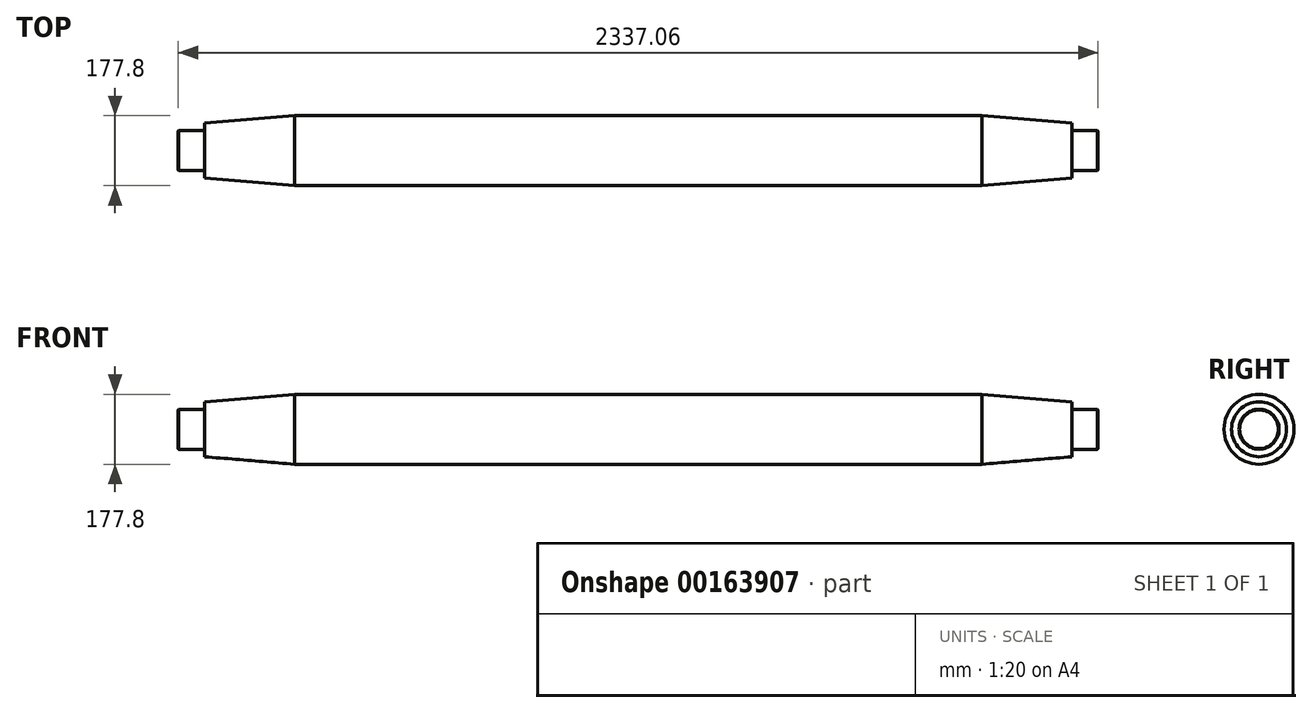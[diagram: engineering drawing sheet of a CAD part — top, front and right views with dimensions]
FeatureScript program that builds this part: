
annotation { "Feature Type Name" : "Feature", "Feature Type Description" : "" }
export const myFeature = defineFeature(function(context is Context, id is Id, definition is map)
    precondition{}
    {
        {
            var Q0;
            Q0=qCreatedBy(makeId("Right.planeOp"),FACE);
            var sketch = newSketch(context, id + "F0", { "sketchPlane" : qUnion([Q0])});
            skCircle(sketch, "E0", {"center": v(0, 0) * mm, "radius": 88.9 * mm});
            skSolve(sketch);
        }
        {
            var Q0;
            Q0 = qSketchRegion(id + "F0", true);
            extrude(context, id + "F1", {"entities" : qUnion([Q0]), "endBound" : BoundingType.SYMMETRIC, "depth" : 1746.25 * mm});
        }
        {
            var Q0;
            Q0=makeQuery(id+"F1.opExtrude","CAP_FACE",FACE,{"disambiguationData":[OSD([sQuery(id+"F0.wireOp",EDGE,"E0")])],"isStart":false});
            cPlane(context, id + "F2", {"entities" : qUnion([Q0]), "cplaneType" : CPlaneType.OFFSET, "offset" : 228.6 * mm, "width" : 152.4 * mm, "height" : 152.4 * mm});
        }
        {
            var Q0;
            Q0=qCreatedBy(id+"F2.planeOp",FACE);
            var sketch = newSketch(context, id + "F3", { "sketchPlane" : qUnion([Q0])});
            skCircle(sketch, "E1", {"center": v(0, 0) * mm, "radius": 69.85 * mm});
            skSolve(sketch);
        }
        {
            var Q1;
            Q1=makeQuery(id+"F1.opExtrude","CAP_FACE",FACE,{"disambiguationData":[OSD([sQuery(id+"F0.wireOp",EDGE,"E0")])],"isStart":false});
            var Q2;
            Q2=makeQuery(id+"F3.imprint","IMPRINT",FACE,{"disambiguationData":[TD([[makeQuery(id+"F3.imprint","IMPRINT",EDGE,{"derivedFrom":sQuery(id+"F3.wireOp",EDGE,"E1")}),1.0]])]});
            loft(context, id + "F4", {"sheetProfilesArray" : [{ "sheetProfileEntities" : qUnion([Q1]) }, { "sheetProfileEntities" : qUnion([Q2]) }]});
        }
        {
            var Q0;
            Q0=makeQuery(id+"F4.opLoft","CAP_FACE",FACE,{"disambiguationData":[OSD([makeQuery(id+"F3.imprint","IMPRINT",FACE,{"disambiguationData":[TD([[makeQuery(id+"F3.imprint","IMPRINT",EDGE,{"derivedFrom":sQuery(id+"F3.wireOp",EDGE,"E1")}),1.0]])]})])],"isStart":true});
            var sketch = newSketch(context, id + "F5", { "sketchPlane" : qUnion([Q0])});
            skCircle(sketch, "E2", {"center": v(0, 0) * mm, "radius": 50.8 * mm});
            skSolve(sketch);
        }
        {
            var Q0;
            Q0=makeQuery(id+"F5.imprint","IMPRINT",FACE,{"disambiguationData":[TD([[makeQuery(id+"F5.imprint","IMPRINT",EDGE,{"derivedFrom":sQuery(id+"F5.wireOp",EDGE,"E2")}),1.0]])]});
            extrude(context, id + "F6", {"entities" : qUnion([Q0]), "operationType" : NewBodyOperationType.ADD, "depth" : 66.8 * mm});
        }
        {
            var Q0;
            Q0=makeQuery(id+"F6.opExtrude","CAP_FACE",FACE,{"disambiguationData":[OSD([sQuery(id+"F5.wireOp",EDGE,"E2")])],"isStart":false});
            chamfer(context, id + "F7", {"entities" : qUnion([Q0]), "width" : 1.52 * mm, "tangentPropagation" : true});
        }
        {
            var Q0;
            Q0=makeQuery(id+"F4.opLoft","SWEPT_BODY",BODY,{"disambiguationData":[OSD([sQuery(id+"F0.wireOp",EDGE,"E0"),makeQuery(id+"F3.imprint","IMPRINT",FACE,{"disambiguationData":[TD([[makeQuery(id+"F3.imprint","IMPRINT",EDGE,{"derivedFrom":sQuery(id+"F3.wireOp",EDGE,"E1")}),1.0]])]})])]});
            var Q1;
            Q1=qCreatedBy(makeId("Right.planeOp"),FACE);
            mirror(context, id + "F8", {"operationType" : NewBodyOperationType.ADD, "entities" : qUnion([Q0]), "mirrorPlane" : qUnion([Q1])});
        }
    });
